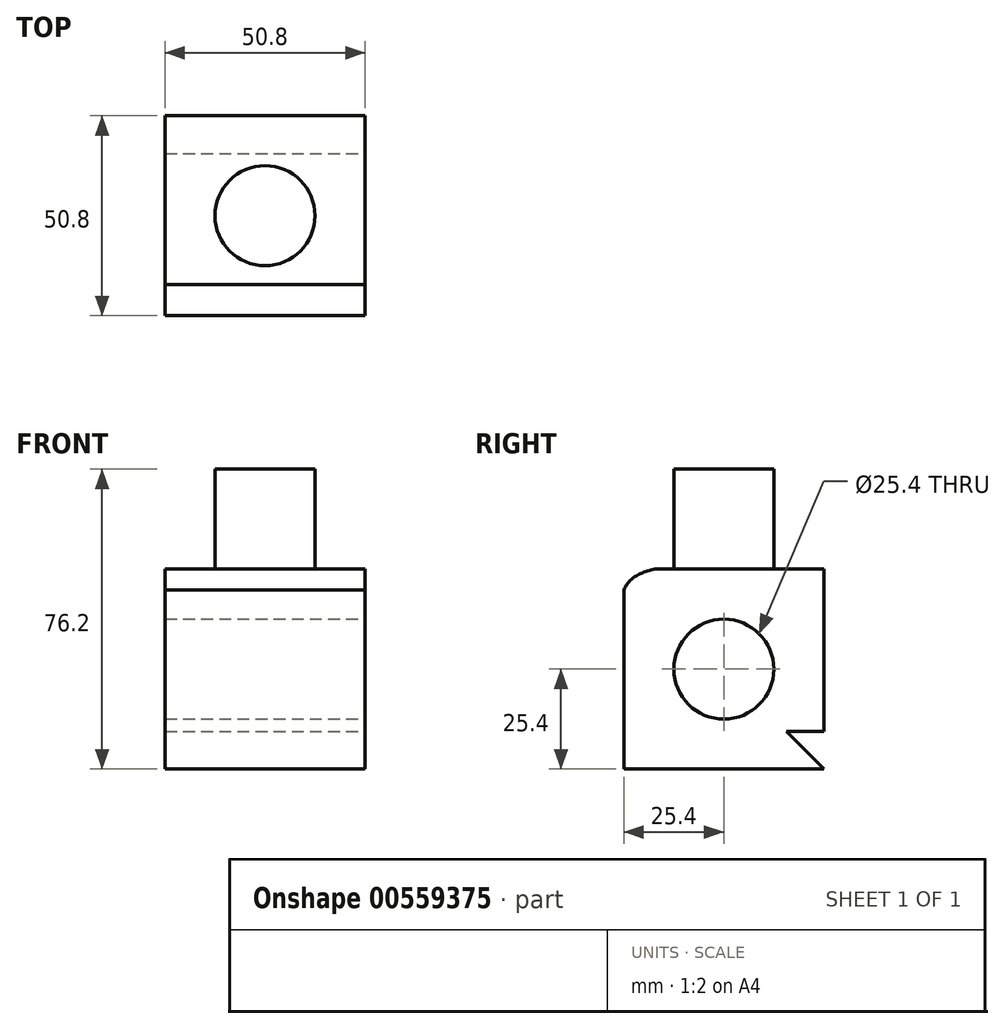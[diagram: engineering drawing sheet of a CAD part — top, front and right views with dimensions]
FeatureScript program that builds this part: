
annotation { "Feature Type Name" : "Feature", "Feature Type Description" : "" }
export const myFeature = defineFeature(function(context is Context, id is Id, definition is map)
    precondition{}
    {
        {
            var Q0;
            Q0=qCreatedBy(makeId("Top.planeOp"),FACE);
            var sketch = newSketch(context, id + "F0", { "sketchPlane" : qUnion([Q0])});
            skLineSegment(sketch, "E0.bottom", {"start": v(25.4, 25.4) * mm, "end": v(-25.4, 25.4) * mm});
            skLineSegment(sketch, "E0.top", {"start": v(25.4, -25.4) * mm, "end": v(-25.4, -25.4) * mm});
            skLineSegment(sketch, "E0.left", {"start": v(25.4, 25.4) * mm, "end": v(25.4, -25.4) * mm});
            skLineSegment(sketch, "E0.right", {"start": v(-25.4, 25.4) * mm, "end": v(-25.4, -25.4) * mm});
            skPoint(sketch, "E0.middle", {"position": v(0, 0) * mm});
            skSolve(sketch);
        }
        {
            var Q0;
            Q0=makeQuery(id+"F0.imprint","IMPRINT",FACE,{"disambiguationData":[TD([[makeQuery(id+"F0.imprint","IMPRINT",EDGE,{"derivedFrom":sQuery(id+"F0.wireOp",EDGE,"E0.bottom")}),1.0]])]});
            extrude(context, id + "F1", {"entities" : qUnion([Q0]), "depth" : 50.8 * mm, "offsetDistance" : 25.4 * mm});
        }
        {
            var Q0;
            Q0=makeQuery(id+"F1.opExtrude","CAP_FACE",FACE,{"disambiguationData":[OSD([sQuery(id+"F0.wireOp",EDGE,"E0.bottom"),sQuery(id+"F0.wireOp",EDGE,"E0.top"),sQuery(id+"F0.wireOp",EDGE,"E0.left"),sQuery(id+"F0.wireOp",EDGE,"E0.right")])],"isStart":false});
            var sketch = newSketch(context, id + "F2", { "sketchPlane" : qUnion([Q0])});
            skCircle(sketch, "E1", {"center": v(0, 0) * mm, "radius": 12.7 * mm});
            skSolve(sketch);
        }
        {
            var Q0;
            Q0=makeQuery(id+"F2.imprint","IMPRINT",FACE,{"disambiguationData":[TD([[makeQuery(id+"F2.imprint","IMPRINT",EDGE,{"derivedFrom":sQuery(id+"F2.wireOp",EDGE,"E1")}),1.0]])]});
            extrude(context, id + "F3", {"entities" : qUnion([Q0]), "operationType" : NewBodyOperationType.ADD, "depth" : 25.4 * mm, "offsetDistance" : 25.4 * mm});
        }
        {
            var Q0;
            Q0=makeQuery(id+"F1.opExtrude","SWEPT_FACE",FACE,{"disambiguationData":[OSD([sQuery(id+"F0.wireOp",EDGE,"E0.left")])]});
            var sketch = newSketch(context, id + "F4", { "sketchPlane" : qUnion([Q0])});
            skCircle(sketch, "E2", {"center": v(0, 25.4) * mm, "radius": 12.7 * mm});
            skSolve(sketch);
        }
        {
            var Q0;
            Q0=makeQuery(id+"F4.imprint","IMPRINT",FACE,{"disambiguationData":[TD([[makeQuery(id+"F4.imprint","IMPRINT",EDGE,{"derivedFrom":sQuery(id+"F4.wireOp",EDGE,"E2")}),1.0]])]});
            extrude(context, id + "F5", {"entities" : qUnion([Q0]), "operationType" : NewBodyOperationType.REMOVE, "oppositeDirection" : true, "depth" : 99.06 * mm, "offsetDistance" : 25.4 * mm});
        }
        {
            var Q0;
            Q0=makeQuery(id+"F1.opExtrude","SWEPT_FACE",FACE,{"disambiguationData":[OSD([sQuery(id+"F0.wireOp",EDGE,"E0.left")])]});
            var sketch = newSketch(context, id + "F6", { "sketchPlane" : qUnion([Q0])});
            skLineSegment(sketch, "E3", {"start": v(-25.4, 50.8) * mm, "end": v(25.4, 0) * mm});
            skLineSegment(sketch, "E4", {"start": v(15.84, 9.56) * mm, "end": v(25.4, 9.56) * mm});
            skSolve(sketch);
        }
        {
            var Q0;
            {var subQ4=sQuery(id+"F6.wireOp",EDGE,"E4");Q0=makeQuery(id+"F6.imprint","IMPRINT",FACE,{"disambiguationData":[TD([[makeQuery(id+"F6.imprint","IMPRINT",EDGE,{"derivedFrom":subQ4}),-1.0]])]});}
            extrude(context, id + "F7", {"entities" : qUnion([Q0]), "operationType" : NewBodyOperationType.REMOVE, "oppositeDirection" : true, "depth" : 60.45 * mm, "offsetDistance" : 25.4 * mm});
        }
        {
            var Q0;
            Q0=makeQuery(id+"F1.opExtrude","SWEPT_FACE",FACE,{"disambiguationData":[OSD([sQuery(id+"F0.wireOp",EDGE,"E0.left")])]});
            var sketch = newSketch(context, id + "F8", { "sketchPlane" : qUnion([Q0])});
            skFitSpline(sketch, "E5", {"points": [v(-25.4, 25.4) * mm, v(-23.92, 47.77) * mm, v(0, 50.8) * mm], "startDerivative": vector(-7.78, 55.3) * mm, "endDerivative": vector(58.18, -4.14) * mm});
            skSolve(sketch);
        }
        {
            var Q0;
            {var subQ0=sQuery(id+"F8.wireOp",EDGE,"E5");var subQ1=sQuery(id+"F0.wireOp",EDGE,"E0.left");var subQ4=makeQuery(id+"F1.opExtrude","CAP_EDGE",EDGE,{"disambiguationData":[OSD([subQ1])],"isStart":false});var subQ5=makeQuery(id+"F8.imprint","INTERSECT",VERTEX,{"disambiguationData":[OD(1.0)],"derivedFrom":[subQ4,subQ0]});Q0=makeQuery(id+"F8.imprint","IMPRINT",FACE,{"disambiguationData":[TD([[makeQuery(id+"F8.imprint","IMPRINT",EDGE,{"disambiguationData":[TD([[subQ5,1.0]])],"derivedFrom":subQ0}),1.0]])]});}
            extrude(context, id + "F9", {"entities" : qUnion([Q0]), "operationType" : NewBodyOperationType.REMOVE, "oppositeDirection" : true, "depth" : 52.78 * mm, "offsetDistance" : 25.4 * mm});
        }
    });
